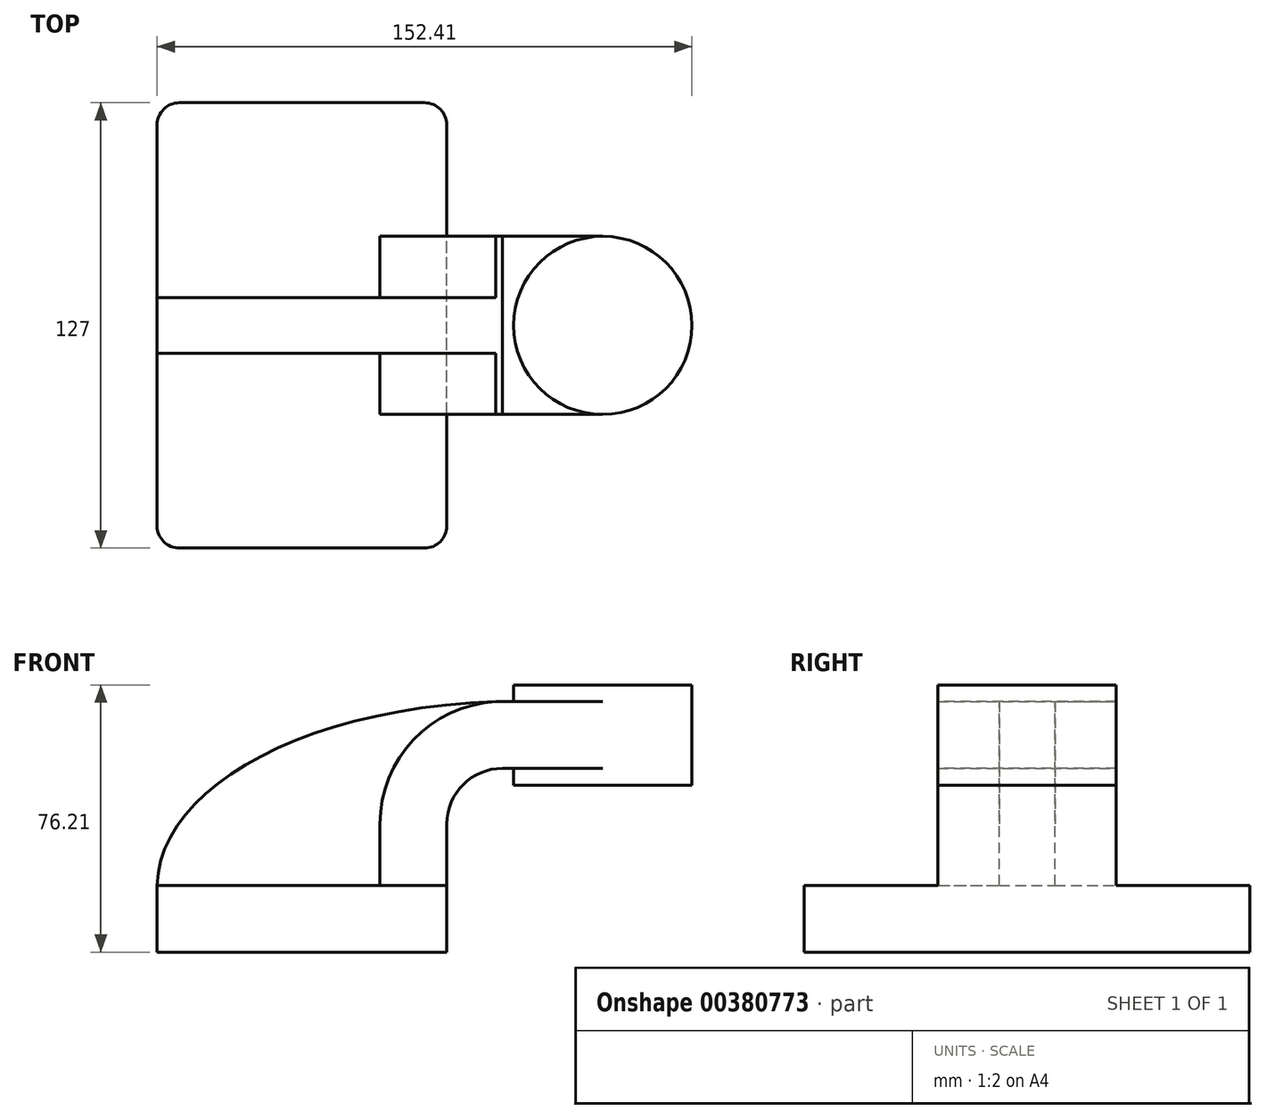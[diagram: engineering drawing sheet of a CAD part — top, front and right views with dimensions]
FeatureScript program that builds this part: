
annotation { "Feature Type Name" : "Feature", "Feature Type Description" : "" }
export const myFeature = defineFeature(function(context is Context, id is Id, definition is map)
    precondition{}
    {
        {
            var Q0;
            Q0=qCreatedBy(makeId("Front.planeOp"),FACE);
            var sketch = newSketch(context, id + "F0", { "sketchPlane" : qUnion([Q0])});
            skLineSegment(sketch, "E0.bottom", {"start": v(-41.28, -9.53) * mm, "end": v(41.28, -9.53) * mm});
            skLineSegment(sketch, "E0.top", {"start": v(-41.28, 9.52) * mm, "end": v(41.28, 9.52) * mm});
            skLineSegment(sketch, "E0.left", {"start": v(-41.28, -9.53) * mm, "end": v(-41.28, 9.52) * mm});
            skLineSegment(sketch, "E0.right", {"start": v(41.28, -9.53) * mm, "end": v(41.28, 9.52) * mm});
            skPoint(sketch, "E0.middle", {"position": v(0, 0) * mm});
            skLineSegment(sketch, "E1.bottom", {"start": v(60.33, 38.1) * mm, "end": v(111.13, 38.1) * mm});
            skLineSegment(sketch, "E1.top", {"start": v(60.32, 66.68) * mm, "end": v(111.13, 66.68) * mm});
            skLineSegment(sketch, "E1.left", {"start": v(60.33, 38.1) * mm, "end": v(60.33, 66.68) * mm});
            skLineSegment(sketch, "E1.right", {"start": v(111.13, 38.1) * mm, "end": v(111.13, 66.68) * mm});
            skPoint(sketch, "E1.middle", {"position": v(85.72, 52.39) * mm});
            skLineSegment(sketch, "E2", {"start": v(41.28, 9.52) * mm, "end": v(41.28, 27) * mm});
            skArc(sketch, "E3", {"start": v(41.27, 27) * mm, "mid": v(45.92, 38.23) * mm, "end": v(57.15, 42.88) * mm});
            skLineSegment(sketch, "E4", {"start": v(57.15, 42.88) * mm, "end": v(85.72, 42.88) * mm});
            skLineSegment(sketch, "E5.0", {"start": v(57.15, 61.93) * mm, "end": v(85.72, 61.93) * mm});
            skArc(sketch, "E5.1", {"start": v(22.22, 27) * mm, "mid": v(32.45, 51.7) * mm, "end": v(57.15, 61.93) * mm});
            skLineSegment(sketch, "E5.2", {"start": v(22.22, 9.52) * mm, "end": v(22.22, 27) * mm});
            skLineSegment(sketch, "E6", {"start": v(85.72, 61.93) * mm, "end": v(85.72, 66.68) * mm});
            skLineSegment(sketch, "E7", {"start": v(85.72, 61.93) * mm, "end": v(85.73, 38.1) * mm});
            skFitSpline(sketch, "E8", {"points": [v(-41.28, 9.52) * mm, v(57.15, 61.93) * mm], "startDerivative": vector(1.76, 81.9) * mm, "endDerivative": vector(171.45, 4.05) * mm});
            skSolve(sketch);
        }
        {
            var Q0;
            Q0=makeQuery(id+"F0.imprint","IMPRINT",FACE,{"disambiguationData":[TD([[makeQuery(id+"F0.imprint","IMPRINT",EDGE,{"derivedFrom":sQuery(id+"F0.wireOp",EDGE,"E0.bottom")}),1.0]])]});
            extrude(context, id + "F1", {"entities" : qUnion([Q0]), "endBound" : BoundingType.SYMMETRIC, "depth" : 127 * mm});
        }
        {
            var Q0;
            {var subQ1=sQuery(id+"F0.wireOp",EDGE,"E2");Q0=makeQuery(id+"F0.imprint","IMPRINT",FACE,{"disambiguationData":[TD([[makeQuery(id+"F0.imprint","IMPRINT",EDGE,{"derivedFrom":subQ1}),1.0]])]});}
            var Q1;
            {var subQ0=sQuery(id+"F0.wireOp",EDGE,"E4");var subQ1=sQuery(id+"F0.wireOp",EDGE,"E1.left");var subQ2=makeQuery(id+"F0.imprint","INTERSECT",VERTEX,{"derivedFrom":[subQ1,subQ0]});Q1=makeQuery(id+"F0.imprint","IMPRINT",FACE,{"disambiguationData":[TD([[makeQuery(id+"F0.imprint","IMPRINT",EDGE,{"disambiguationData":[TD([[subQ2,-1.0]])],"derivedFrom":subQ1}),-1.0]])]});}
            extrude(context, id + "F2", {"entities" : qUnion([Q0, Q1]), "operationType" : NewBodyOperationType.ADD, "endBound" : BoundingType.SYMMETRIC, "depth" : 50.8 * mm});
        }
        {
            var Q0;
            {var subQ3=sQuery(id+"F0.wireOp",EDGE,"E5.2");Q0=makeQuery(id+"F0.imprint","IMPRINT",FACE,{"disambiguationData":[TD([[makeQuery(id+"F0.imprint","IMPRINT",EDGE,{"derivedFrom":subQ3}),1.0]])]});}
            extrude(context, id + "F3", {"entities" : qUnion([Q0]), "operationType" : NewBodyOperationType.ADD, "endBound" : BoundingType.SYMMETRIC, "depth" : 15.88 * mm});
        }
        {
            var Q0;
            {var subQ1=sQuery(id+"F0.wireOp",EDGE,"E1.right");Q0=makeQuery(id+"F0.imprint","IMPRINT",FACE,{"disambiguationData":[TD([[makeQuery(id+"F0.imprint","IMPRINT",EDGE,{"derivedFrom":subQ1}),1.0]])]});}
            var Q1;
            Q1=sQuery(id+"F0.wireOp",EDGE,"E7");
            revolve(context, id + "F4", {"operationType" : NewBodyOperationType.ADD, "entities" : qUnion([Q0]), "axis" : qUnion([Q1]), "revolveType" : RevolveType.FULL});
        }
        {
            var Q0;
            Q0=makeQuery(id+"F1.opExtrude","CAP_EDGE",EDGE,{"disambiguationData":[OSD([sQuery(id+"F0.wireOp",EDGE,"E0.right")])],"isStart":false});
            var Q1;
            Q1=makeQuery(id+"F1.opExtrude","CAP_EDGE",EDGE,{"disambiguationData":[OSD([sQuery(id+"F0.wireOp",EDGE,"E0.left")])],"isStart":false});
            var Q2;
            Q2=makeQuery(id+"F1.opExtrude","CAP_EDGE",EDGE,{"disambiguationData":[OSD([sQuery(id+"F0.wireOp",EDGE,"E0.left")])],"isStart":true});
            var Q3;
            Q3=makeQuery(id+"F1.opExtrude","CAP_EDGE",EDGE,{"disambiguationData":[OSD([sQuery(id+"F0.wireOp",EDGE,"E0.right")])],"isStart":true});
            fillet(context, id + "F5", {"entities" : qUnion([Q0, Q1, Q2, Q3]), "radius" : 6.35 * mm, "tangentPropagation" : true, "allowEdgeOverflow" : false});
        }
    });
